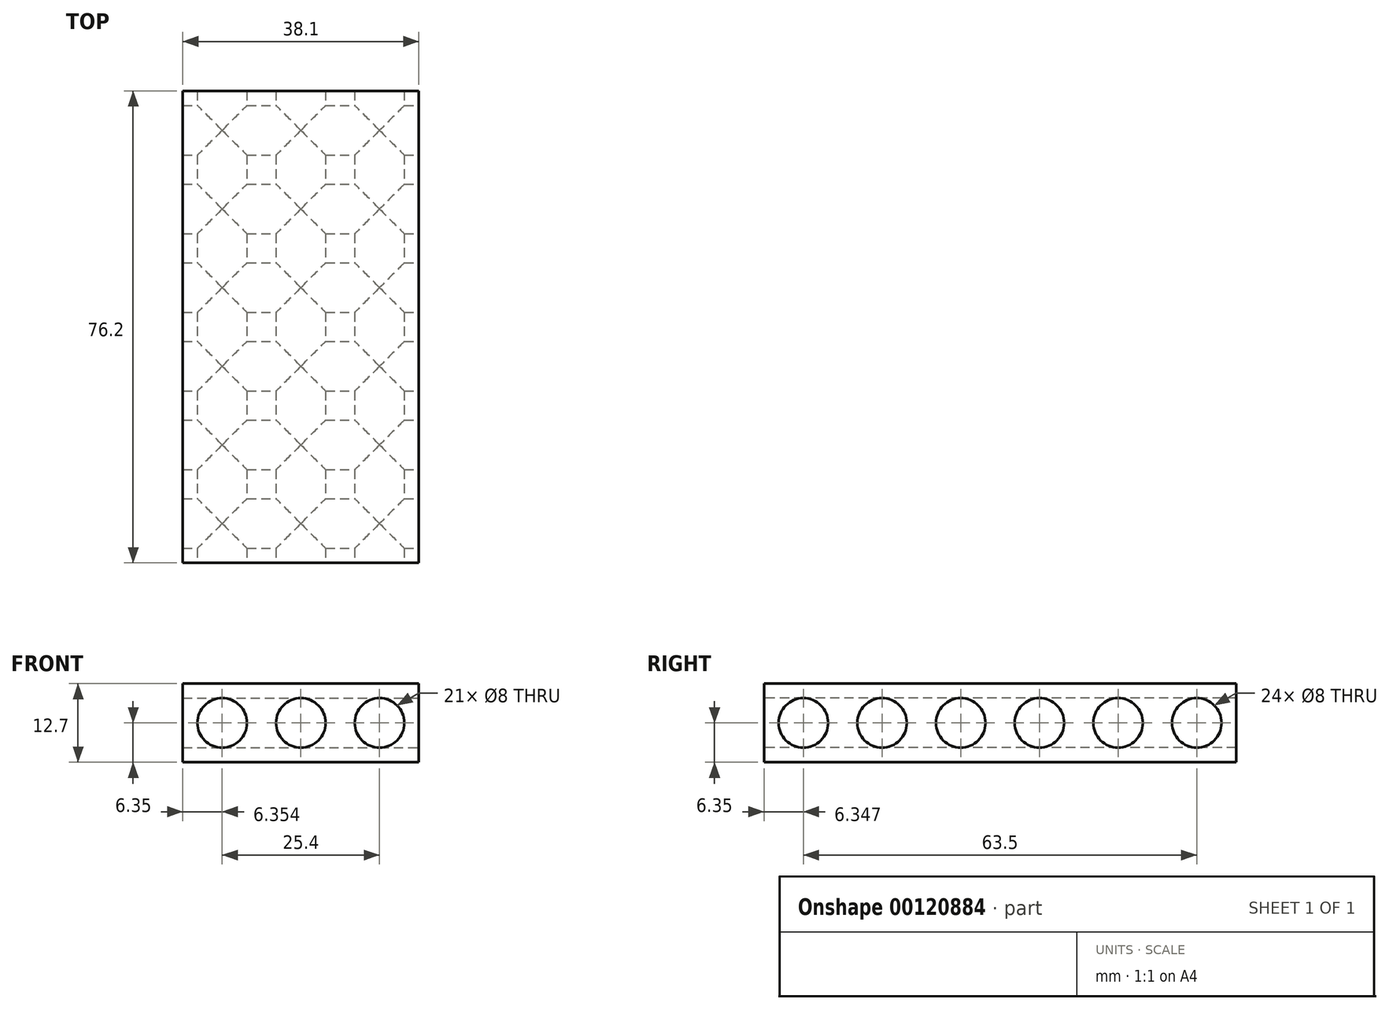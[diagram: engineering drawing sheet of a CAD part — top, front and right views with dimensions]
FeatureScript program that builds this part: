
annotation { "Feature Type Name" : "Feature", "Feature Type Description" : "" }
export const myFeature = defineFeature(function(context is Context, id is Id, definition is map)
    precondition{}
    {
        {
            var Q0;
            Q0=qCreatedBy(makeId("Top.planeOp"),FACE);
            var sketch = newSketch(context, id + "F0", { "sketchPlane" : qUnion([Q0])});
            skLineSegment(sketch, "E0.bottom", {"start": v(-35.06, 35.59) * mm, "end": v(3.04, 35.59) * mm});
            skLineSegment(sketch, "E0.top", {"start": v(-35.06, -40.61) * mm, "end": v(3.04, -40.61) * mm});
            skLineSegment(sketch, "E0.left", {"start": v(-35.06, 35.59) * mm, "end": v(-35.06, -40.61) * mm});
            skLineSegment(sketch, "E0.right", {"start": v(3.04, 35.59) * mm, "end": v(3.04, -40.61) * mm});
            skSolve(sketch);
        }
        {
            var Q0;
            Q0 = qSketchRegion(id + "F0", true);
            extrude(context, id + "F1", {"entities" : qUnion([Q0]), "depth" : 12.7 * mm});
        }
        {
            var Q0;
            Q0=makeQuery(id+"F1.opExtrude","SWEPT_FACE",FACE,{"disambiguationData":[OSD([sQuery(id+"F0.wireOp",EDGE,"E0.right")])]});
            var sketch = newSketch(context, id + "F2", { "sketchPlane" : qUnion([Q0])});
            skCircle(sketch, "E1", {"center": v(-34.26, 6.35) * mm, "radius": 4 * mm});
            skCircle(sketch, "E2.1.0.0", {"center": v(-21.56, 6.35) * mm, "radius": 4 * mm});
            skCircle(sketch, "E2.2.0.0", {"center": v(-8.86, 6.35) * mm, "radius": 4 * mm});
            skCircle(sketch, "E2.3.0.0", {"center": v(3.84, 6.35) * mm, "radius": 4 * mm});
            skCircle(sketch, "E2.4.0.0", {"center": v(16.54, 6.35) * mm, "radius": 4 * mm});
            skCircle(sketch, "E2.5.0.0", {"center": v(29.24, 6.35) * mm, "radius": 4 * mm});
            skLineSegment(sketch, "E2.direction1", {"start": v(-34.26, 6.35) * mm, "end": v(-21.56, 6.35) * mm, "construction": true});
            skSolve(sketch);
        }
        {
            var Q0;
            Q0 = qSketchRegion(id + "F2", true);
            extrude(context, id + "F3", {"entities" : qUnion([Q0]), "operationType" : NewBodyOperationType.REMOVE, "endBound" : BoundingType.THROUGH_ALL, "oppositeDirection" : true, "depth" : 25 * mm});
        }
        {
            var Q0;
            Q0=makeQuery(id+"F1.opExtrude","SWEPT_FACE",FACE,{"disambiguationData":[OSD([sQuery(id+"F0.wireOp",EDGE,"E0.top")])]});
            var sketch = newSketch(context, id + "F4", { "sketchPlane" : qUnion([Q0])});
            skCircle(sketch, "E3", {"center": v(-28.7, 6.35) * mm, "radius": 4 * mm});
            skCircle(sketch, "E4.1.0.0", {"center": v(-16, 6.35) * mm, "radius": 4 * mm});
            skCircle(sketch, "E4.2.0.0", {"center": v(-3.3, 6.35) * mm, "radius": 4 * mm});
            skLineSegment(sketch, "E4.direction1", {"start": v(-28.7, 6.35) * mm, "end": v(-16, 6.35) * mm, "construction": true});
            skSolve(sketch);
        }
        {
            var Q0;
            Q0 = qSketchRegion(id + "F4", true);
            extrude(context, id + "F5", {"entities" : qUnion([Q0]), "operationType" : NewBodyOperationType.REMOVE, "endBound" : BoundingType.THROUGH_ALL, "oppositeDirection" : true, "depth" : 25 * mm});
        }
    });
